# Revit family: CEMCO-VIPER-X_VXS
name_source: partatom
category: Structural Columns
units: mm (PartAtom-declared; Revit-internal decimal feet)

## family parameters
Always export as geometry = No
Beam cutback in plan = From geometry
Cut with Voids When Loaded = No
Material for Model Behavior = Steel
Section Shape = Not Defined
Shared = No
Show family pre-cut in plan views = Yes

## types (2) — shared parameters
Manufacturer = CEMCO
Model = V2
OP = 0' - 0 1/16"
OPH = 0' - 0 5/16"
Product Info = Viper-X Studs
Product Submittal Link = https://cemcosteel.com
RW = 0' - 0 1/8"
Return = 0' - 0 3/8"
URL = https://cemcosteel.com
Xcg = 0' - 0 23/32"
bf = 0' - 1 7/16"
d = 0' - 1 5/8"
fy = 50
r = 0' - 0 1/32"
temp_tf = 0' - 0 1/32"
tf = 0' - 0 1/32"

## per-type parameters (varying)
| type | Assembly Code | Description | Keynote |
| Default |  | CEMCO Interior Non-Load Bearing |  |
| 600VXT125-22 | C1010100 | CEMCO Interior Non-Load Bearing Wall Studs | 092216 |

## geometry (parser evidence)
native form markers: Sweep x4
no freeform markers — native parametric forms only
